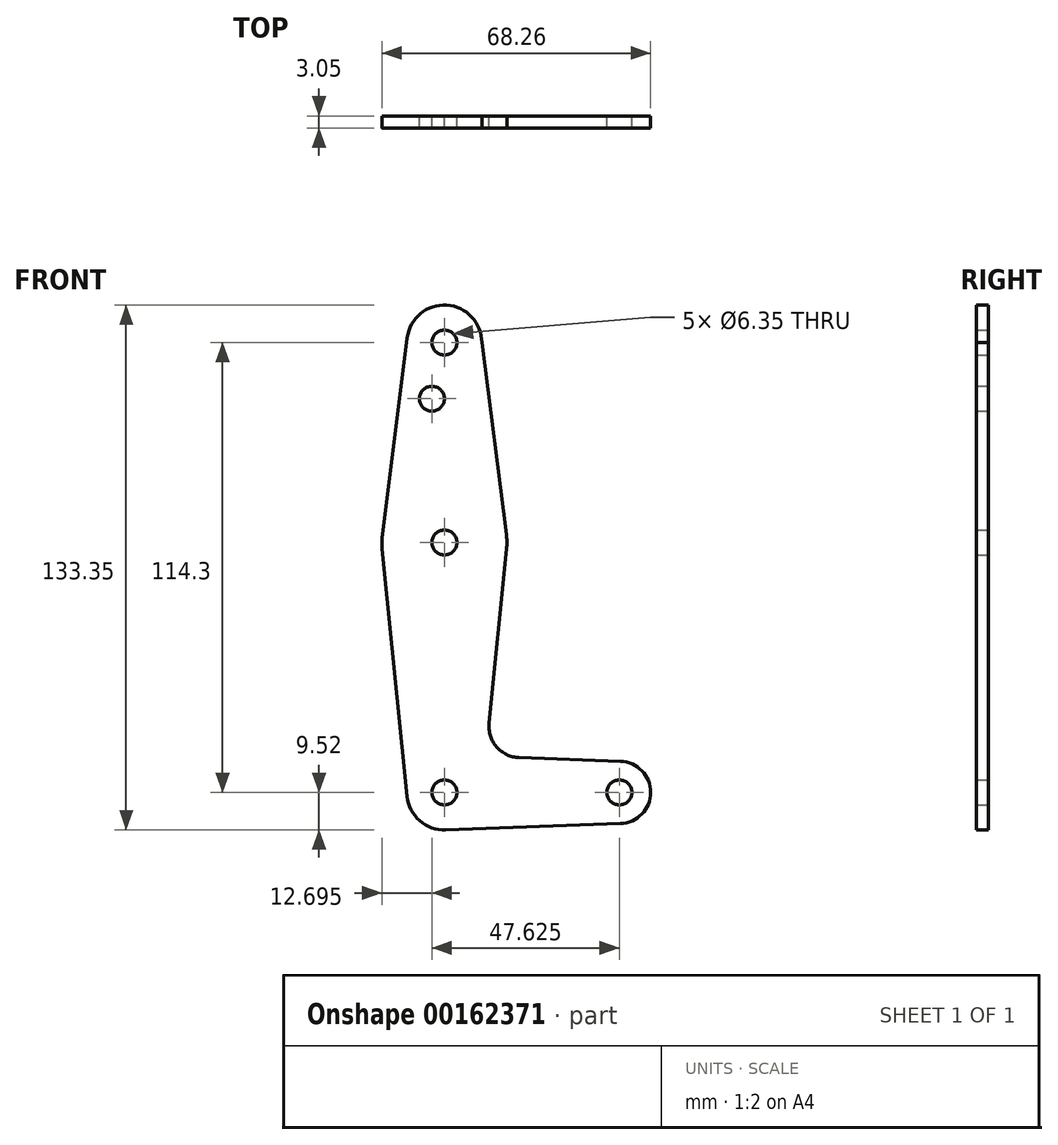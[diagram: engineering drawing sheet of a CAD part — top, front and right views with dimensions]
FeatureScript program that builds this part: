
annotation { "Feature Type Name" : "Feature", "Feature Type Description" : "" }
export const myFeature = defineFeature(function(context is Context, id is Id, definition is map)
    precondition{}
    {
        {
            var Q0;
            Q0=qCreatedBy(makeId("Front.planeOp"),FACE);
            var sketch = newSketch(context, id + "F0", { "sketchPlane" : qUnion([Q0])});
            skLineSegment(sketch, "E0", {"start": v(0, 0) * mm, "end": v(0, 114.3) * mm, "construction": true});
            skLineSegment(sketch, "E1", {"start": v(0, 0) * mm, "end": v(44.45, 0) * mm, "construction": true});
            skCircle(sketch, "E2", {"center": v(0, 114.3) * mm, "radius": 9.53 * mm});
            skCircle(sketch, "E3", {"center": v(0, 63.5) * mm, "radius": 15.88 * mm});
            skCircle(sketch, "E4", {"center": v(0, 0) * mm, "radius": 9.53 * mm});
            skCircle(sketch, "E5", {"center": v(44.45, 0) * mm, "radius": 7.94 * mm});
            skLineSegment(sketch, "E6", {"start": v(-9.45, 115.5) * mm, "end": v(-15.75, 65.48) * mm});
            skLineSegment(sketch, "E7", {"start": v(9.53, 114.3) * mm, "end": v(15.75, 65.5) * mm});
            skLineSegment(sketch, "E8", {"start": v(-15.8, 61.91) * mm, "end": v(-9.48, -0.95) * mm});
            skLineSegment(sketch, "E9", {"start": v(15.8, 61.91) * mm, "end": v(11.34, 17.6) * mm});
            skLineSegment(sketch, "E10", {"start": v(18.97, 8.85) * mm, "end": v(44.73, 7.93) * mm});
            skLineSegment(sketch, "E11", {"start": v(0.34, -9.52) * mm, "end": v(44.73, -7.93) * mm});
            skCircle(sketch, "E12", {"center": v(0, 114.3) * mm, "radius": 3.18 * mm});
            skCircle(sketch, "E13", {"center": v(0, 63.5) * mm, "radius": 3.18 * mm});
            skCircle(sketch, "E14", {"center": v(0, 0) * mm, "radius": 3.18 * mm});
            skCircle(sketch, "E15", {"center": v(44.45, 0) * mm, "radius": 3.18 * mm});
            skCircle(sketch, "E16", {"center": v(-3.18, 100.03) * mm, "radius": 3.18 * mm});
            skArc(sketch, "E17.filletArc", {"start": v(11.34, 17.6) * mm, "mid": v(13.26, 11.57) * mm, "end": v(18.97, 8.85) * mm});
            skSolve(sketch);
        }
        {
            var Q0;
            Q0 = qSketchRegion(id + "F0", true);
            extrude(context, id + "F1", {"entities" : qUnion([Q0]), "depth" : 3.05 * mm});
        }
    });
